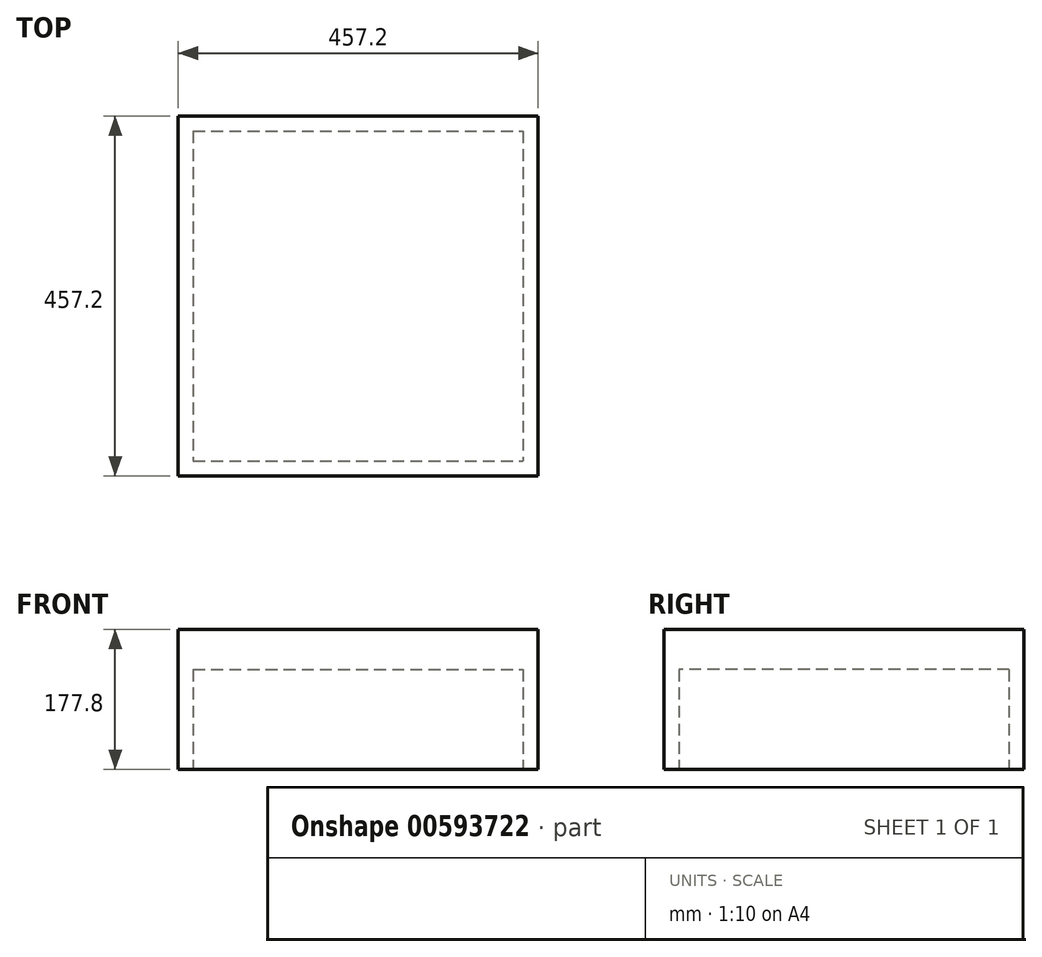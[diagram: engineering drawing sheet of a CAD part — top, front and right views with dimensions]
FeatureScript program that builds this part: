
annotation { "Feature Type Name" : "Feature", "Feature Type Description" : "" }
export const myFeature = defineFeature(function(context is Context, id is Id, definition is map)
    precondition{}
    {
        {
            var Q0;
            Q0=qCreatedBy(makeId("Top.planeOp"),FACE);
            var sketch = newSketch(context, id + "F0", { "sketchPlane" : qUnion([Q0])});
            skLineSegment(sketch, "E0.bottom", {"start": v(-235.9, 258.33) * mm, "end": v(221.3, 258.33) * mm});
            skLineSegment(sketch, "E0.top", {"start": v(-235.9, -198.87) * mm, "end": v(221.3, -198.87) * mm});
            skLineSegment(sketch, "E0.left", {"start": v(-235.9, 258.33) * mm, "end": v(-235.9, -198.87) * mm});
            skLineSegment(sketch, "E0.right", {"start": v(221.3, 258.33) * mm, "end": v(221.3, -198.87) * mm});
            skLineSegment(sketch, "E1.0", {"start": v(202.26, 239.28) * mm, "end": v(202.26, -179.82) * mm});
            skLineSegment(sketch, "E1.1", {"start": v(-216.84, 239.28) * mm, "end": v(202.26, 239.28) * mm});
            skLineSegment(sketch, "E1.2", {"start": v(-216.84, 239.28) * mm, "end": v(-216.84, -179.82) * mm});
            skLineSegment(sketch, "E1.3", {"start": v(-216.84, -179.82) * mm, "end": v(202.26, -179.82) * mm});
            skSolve(sketch);
        }
        {
            var Q0;
            Q0=makeQuery(id+"F0.imprint","IMPRINT",FACE,{"disambiguationData":[TD([[makeQuery(id+"F0.imprint","IMPRINT",EDGE,{"derivedFrom":sQuery(id+"F0.wireOp",EDGE,"E0.bottom")}),-1.0]])]});
            extrude(context, id + "F1", {"entities" : qUnion([Q0]), "depth" : 127 * mm, "offsetDistance" : 25.4 * mm});
        }
        {
            var Q0;
            Q0=makeQuery(id+"F1.opExtrude","CAP_FACE",FACE,{"disambiguationData":[OSD([sQuery(id+"F0.wireOp",EDGE,"E0.bottom"),sQuery(id+"F0.wireOp",EDGE,"E0.top"),sQuery(id+"F0.wireOp",EDGE,"E0.left"),sQuery(id+"F0.wireOp",EDGE,"E0.right"),sQuery(id+"F0.wireOp",EDGE,"E1.0"),sQuery(id+"F0.wireOp",EDGE,"E1.1"),sQuery(id+"F0.wireOp",EDGE,"E1.2"),sQuery(id+"F0.wireOp",EDGE,"E1.3")])],"isStart":false});
            var sketch = newSketch(context, id + "F2", { "sketchPlane" : qUnion([Q0])});
            skLineSegment(sketch, "E2", {"start": v(-239.32, 329.96) * mm, "end": v(-235.9, 258.33) * mm, "construction": true});
            skLineSegment(sketch, "E3", {"start": v(-235.9, 258.33) * mm, "end": v(221.3, -198.87) * mm, "construction": true});
            skLineSegment(sketch, "E4", {"start": v(221.3, -198.87) * mm, "end": v(-235.9, -198.87) * mm});
            skLineSegment(sketch, "E5", {"start": v(-235.9, -198.87) * mm, "end": v(-235.9, 258.33) * mm});
            skLineSegment(sketch, "E6", {"start": v(221.3, 258.33) * mm, "end": v(221.3, -198.87) * mm});
            skLineSegment(sketch, "E7", {"start": v(221.3, 258.33) * mm, "end": v(-235.9, 258.33) * mm});
            skSolve(sketch);
        }
        {
            var Q0;
            Q0 = qSketchRegion(id + "F2", true);
            extrude(context, id + "F3", {"entities" : qUnion([Q0]), "operationType" : NewBodyOperationType.ADD, "depth" : 50.8 * mm, "offsetDistance" : 25.4 * mm});
        }
    });
